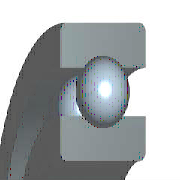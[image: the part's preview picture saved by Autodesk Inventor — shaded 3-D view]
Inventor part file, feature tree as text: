
AUTODESK INVENTOR PART (.ipt)
format: ipt  version: 2023.1 (Build 271208000, 208)  size: 344,064 bytes
history: native  units: mm (DEFAULTED — no unit token found)
features: sketch x5, other x3, plane x2, pattern_circular x1, fillet x1
ambient origin geometry x8: Origin, YZ Plane, XZ Plane, XY Plane, X Axis, Y Axis, Z Axis, Center Point
bodies: Solid1 (feature_tree)
feature tree (12):
  sketch  "Sketch1"  dims[d2=72.0mm]
  other  "WorkPoint1"
  other  "WorkAxis1"
  plane  "WorkPlane3"
  plane  "WorkPlane4"
  sketch  "Sketch4"  dims[d5=12.0mm]
  other  "WorkPoint2"
  pattern_circular  "PolarArray1"  Count=2  [1 undecoded]
  fillet  "Fillet1"  Radius=17.0mm
  sketch  "Sketch2"  dims[d3=40.0mm]
  sketch  "Sketch3"  dims[d4=19.0mm]
  sketch  "Sketch5"  dims[d6=360.0deg d7=0.0mm d8=15.6mm d9=6.9mm d10=360.0deg d11=-12.0mm d12=0.0mm d13=0.0mm d14=15.6001mm d15=6.9001mm d16=360.0deg d17=65.956522mm d19=360.0deg d20=0.6mm d21=12.18mm d22=14.25mm d23=16.32mm d26=0.0mm d27=0.0mm d28=0.0mm d29=0.0mm d30=0.0mm]
note: 1 required parameter value undecoded (feature->parameter linkage not recoverable at this tier; creation-order binding heuristic only, values carry confidence <= 0.55)
